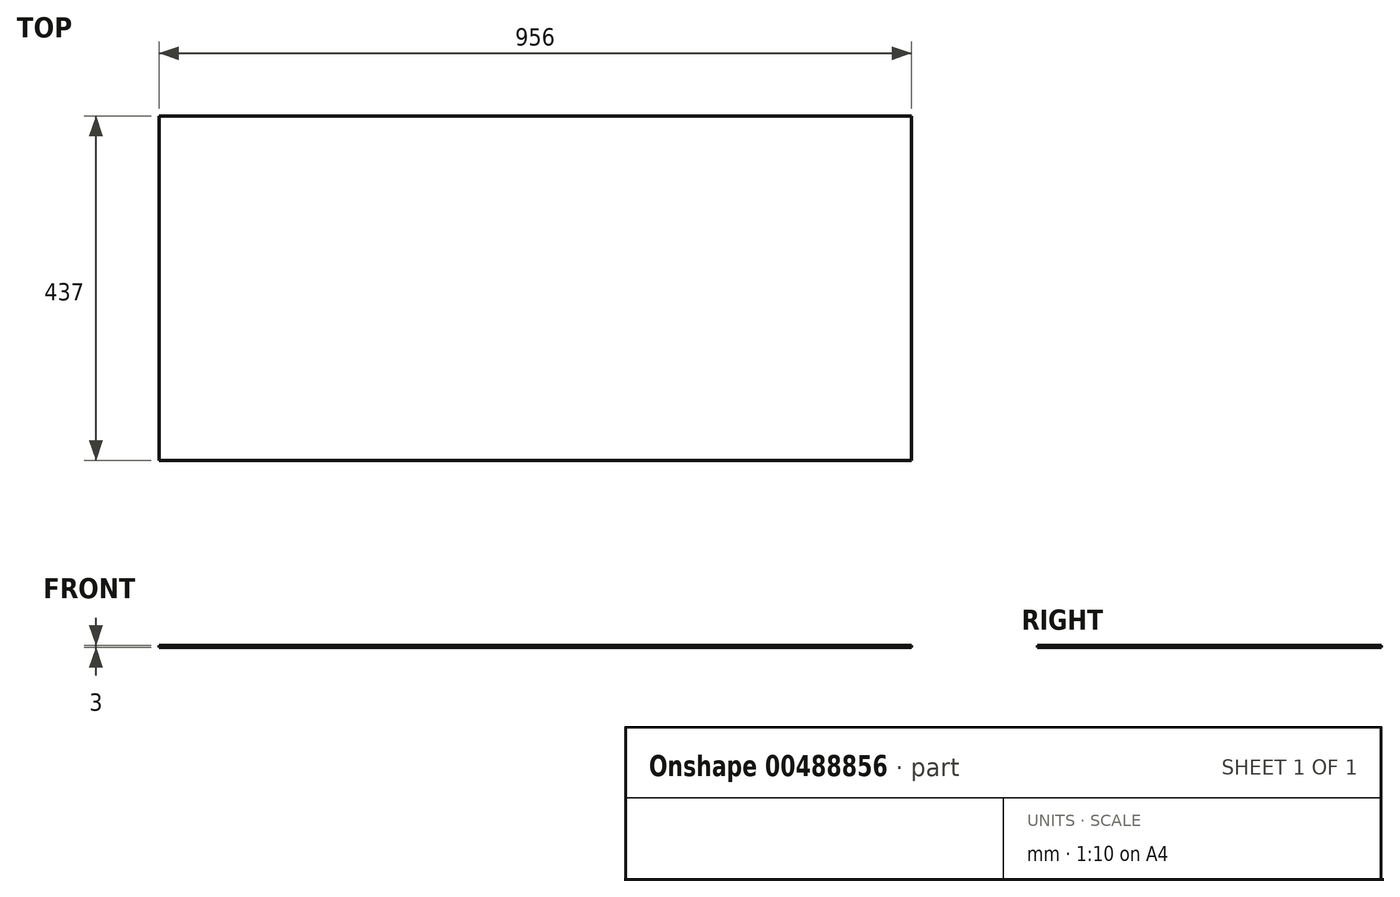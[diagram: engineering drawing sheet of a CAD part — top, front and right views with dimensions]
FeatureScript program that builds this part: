
annotation { "Feature Type Name" : "Feature", "Feature Type Description" : "" }
export const myFeature = defineFeature(function(context is Context, id is Id, definition is map)
    precondition{}
    {
        {
            var Q0;
            Q0=qCreatedBy(makeId("Top.planeOp"),FACE);
            var sketch = newSketch(context, id + "F0", { "sketchPlane" : qUnion([Q0])});
            skLineSegment(sketch, "E0.bottom", {"start": v(-491.1, 185.52) * mm, "end": v(464.9, 185.52) * mm});
            skLineSegment(sketch, "E0.top", {"start": v(-491.1, -251.48) * mm, "end": v(464.9, -251.48) * mm});
            skLineSegment(sketch, "E0.left", {"start": v(-491.1, 185.52) * mm, "end": v(-491.1, -251.48) * mm});
            skLineSegment(sketch, "E0.right", {"start": v(464.9, 185.52) * mm, "end": v(464.9, -251.48) * mm});
            skSolve(sketch);
        }
        {
            var Q0;
            Q0=makeQuery(id+"F0.imprint","IMPRINT",FACE,{"disambiguationData":[TD([[makeQuery(id+"F0.imprint","IMPRINT",EDGE,{"derivedFrom":sQuery(id+"F0.wireOp",EDGE,"E0.bottom")}),-1.0]])]});
            extrude(context, id + "F1", {"entities" : qUnion([Q0]), "depth" : 3 * mm});
        }
    });
